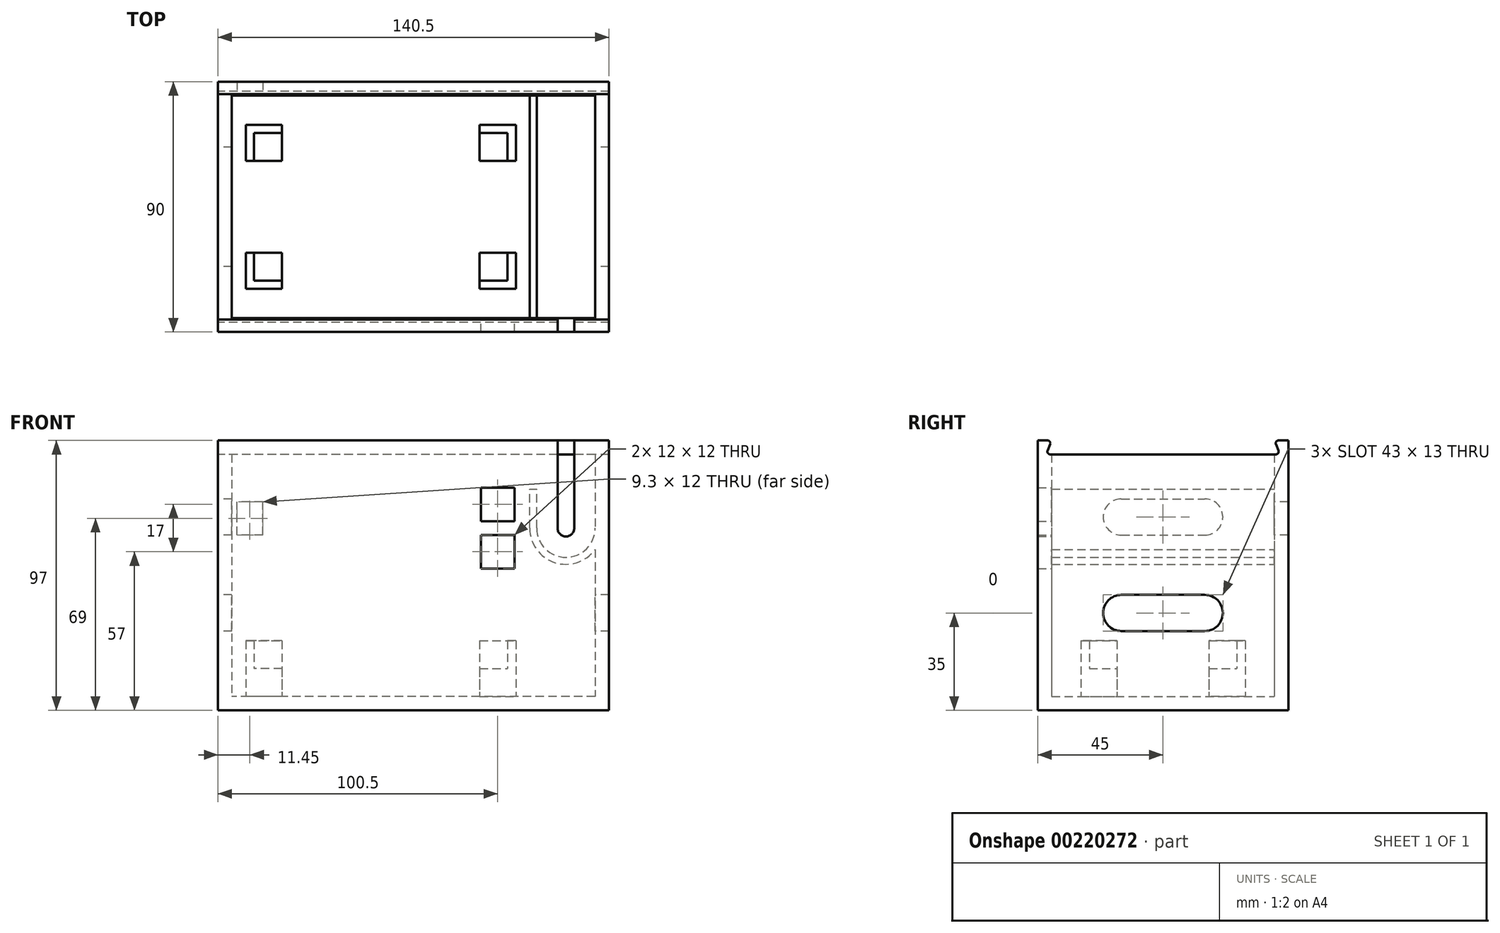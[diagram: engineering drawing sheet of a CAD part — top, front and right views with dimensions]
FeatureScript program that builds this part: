
annotation { "Feature Type Name" : "Feature", "Feature Type Description" : "" }
export const myFeature = defineFeature(function(context is Context, id is Id, definition is map)
    precondition{}
    {
        {
            var Q0;
            Q0=qCreatedBy(makeId("Top.planeOp"),FACE);
            var sketch = newSketch(context, id + "F0", { "sketchPlane" : qUnion([Q0])});
            skLineSegment(sketch, "E0.bottom", {"start": v(70.25, -45) * mm, "end": v(-70.25, -45) * mm});
            skLineSegment(sketch, "E0.top", {"start": v(70.25, 45) * mm, "end": v(-70.25, 45) * mm});
            skLineSegment(sketch, "E0.left", {"start": v(70.25, -45) * mm, "end": v(70.25, 45) * mm});
            skLineSegment(sketch, "E0.right", {"start": v(-70.25, -45) * mm, "end": v(-70.25, 45) * mm});
            skPoint(sketch, "E0.middle", {"position": v(0, 0) * mm});
            skSolve(sketch);
        }
        {
            var Q0;
            Q0=makeQuery(id+"F0.imprint","IMPRINT",FACE,{"disambiguationData":[TD([[makeQuery(id+"F0.imprint","IMPRINT",EDGE,{"derivedFrom":sQuery(id+"F0.wireOp",EDGE,"E0.bottom")}),-1.0]])]});
            extrude(context, id + "F1", {"entities" : qUnion([Q0]), "depth" : 112 * mm});
        }
        {
            var Q0;
            Q0=makeQuery(id+"F1.opExtrude","CAP_FACE",FACE,{"disambiguationData":[OSD([sQuery(id+"F0.wireOp",EDGE,"E0.bottom"),sQuery(id+"F0.wireOp",EDGE,"E0.top"),sQuery(id+"F0.wireOp",EDGE,"E0.left"),sQuery(id+"F0.wireOp",EDGE,"E0.right")])],"isStart":false});
            shell(context, id + "F2", {"entities" : qUnion([Q0]), "thickness" : 5 * mm});
        }
        {
            var Q0;
            Q0=makeQuery(id+"F1.opExtrude","SWEPT_FACE",FACE,{"disambiguationData":[OSD([sQuery(id+"F0.wireOp",EDGE,"E0.right")])]});
            var sketch = newSketch(context, id + "F3", { "sketchPlane" : qUnion([Q0])});
            skLineSegment(sketch, "E1", {"start": v(-40, 107) * mm, "end": v(-40.52, 107) * mm});
            skLineSegment(sketch, "E2", {"start": v(-41.45, 108.37) * mm, "end": v(-40.55, 110.63) * mm});
            skLineSegment(sketch, "E3", {"start": v(40, 107) * mm, "end": v(40.52, 107) * mm});
            skLineSegment(sketch, "E4", {"start": v(41.45, 108.37) * mm, "end": v(40.55, 110.63) * mm});
            skLineSegment(sketch, "E5", {"start": v(-40, 107) * mm, "end": v(40, 107) * mm});
            skArc(sketch, "E6.filletArc", {"start": v(-40.55, 110.63) * mm, "mid": v(-40.65, 111.56) * mm, "end": v(-41.48, 112) * mm});
            skPoint(sketch, "E7.visualSharp", {"position": v(-42, 107) * mm});
            skArc(sketch, "E7.filletArc", {"start": v(-41.45, 108.37) * mm, "mid": v(-41.35, 107.44) * mm, "end": v(-40.52, 107) * mm});
            skArc(sketch, "E8.filletArc", {"start": v(41.48, 112) * mm, "mid": v(40.65, 111.56) * mm, "end": v(40.55, 110.63) * mm});
            skPoint(sketch, "E9.visualSharp", {"position": v(42, 107) * mm});
            skArc(sketch, "E9.filletArc", {"start": v(40.52, 107) * mm, "mid": v(41.35, 107.44) * mm, "end": v(41.45, 108.37) * mm});
            skLineSegment(sketch, "E10", {"start": v(-41.48, 112) * mm, "end": v(41.48, 112) * mm});
            skSolve(sketch);
        }
        {
            var Q0;
            Q0=makeQuery(id+"F3.imprint","IMPRINT",FACE,{"disambiguationData":[TD([[makeQuery(id+"F3.imprint","IMPRINT",EDGE,{"derivedFrom":sQuery(id+"F3.wireOp",EDGE,"E1")}),-1.0]])]});
            extrude(context, id + "F4", {"entities" : qUnion([Q0]), "operationType" : NewBodyOperationType.REMOVE, "oppositeDirection" : true, "depth" : 147.9 * mm});
        }
        {
            var Q0;
            Q0=makeQuery(id+"F2.opShell","OFFSET_FACE",FACE,{"disambiguationData":[OSD([sQuery(id+"F0.wireOp",EDGE,"E0.top")])]});
            var sketch = newSketch(context, id + "F5", { "sketchPlane" : qUnion([Q0])});
            skArc(sketch, "E11", {"start": v(44.25, 80.5) * mm, "mid": v(54.75, 70) * mm, "end": v(65.25, 80.5) * mm});
            skArc(sketch, "E12", {"start": v(41.75, 80.5) * mm, "mid": v(50.72, 68.14) * mm, "end": v(65.25, 72.84) * mm});
            skPoint(sketch, "E13", {"position": v(44.25, 80.5) * mm});
            skPoint(sketch, "E14", {"position": v(41.75, 80.5) * mm});
            skLineSegment(sketch, "E15", {"start": v(44.25, 80.5) * mm, "end": v(44.25, 94.5) * mm});
            skLineSegment(sketch, "E16", {"start": v(41.75, 80.5) * mm, "end": v(41.75, 94.5) * mm});
            skLineSegment(sketch, "E17", {"start": v(41.75, 94.5) * mm, "end": v(44.25, 94.5) * mm});
            skPoint(sketch, "E18", {"position": v(65.25, 80.5) * mm});
            skLineSegment(sketch, "E19", {"start": v(65.25, 80.5) * mm, "end": v(65.25, 72.84) * mm});
            skSolve(sketch);
        }
        {
            var Q0;
            Q0=qSketchRegion(id+"F5",true);
            extrude(context, id + "F6", {"entities" : qUnion([Q0]), "operationType" : NewBodyOperationType.ADD, "depth" : 83.1 * mm});
        }
        {
            var Q0;
            Q0=makeQuery(id+"F2.opShell","OFFSET_FACE",FACE,{"disambiguationData":[OSD([sQuery(id+"F0.wireOp",EDGE,"E0.bottom")])]});
            var sketch = newSketch(context, id + "F7", { "sketchPlane" : qUnion([Q0])});
            skArc(sketch, "E20", {"start": v(-57.75, 80.5) * mm, "mid": v(-54.75, 77.5) * mm, "end": v(-51.75, 80.5) * mm});
            skLineSegment(sketch, "E21", {"start": v(-57.75, 80.5) * mm, "end": v(-57.75, 112.14) * mm});
            skLineSegment(sketch, "E22", {"start": v(-57.75, 112.14) * mm, "end": v(-51.75, 112.14) * mm});
            skLineSegment(sketch, "E23", {"start": v(-51.75, 112.14) * mm, "end": v(-51.75, 80.5) * mm});
            skLineSegment(sketch, "E24", {"start": v(-54.75, 80.5) * mm, "end": v(-36.25, 80.5) * mm});
            skLineSegment(sketch, "E25", {"start": v(-36.25, 80.5) * mm, "end": v(-36.25, 83) * mm});
            skLineSegment(sketch, "E26", {"start": v(-36.25, 80.5) * mm, "end": v(-36.25, 78) * mm});
            skLineSegment(sketch, "E27.bottom", {"start": v(-36.25, 83) * mm, "end": v(-24.25, 83) * mm});
            skLineSegment(sketch, "E27.top", {"start": v(-36.25, 95) * mm, "end": v(-24.25, 95) * mm});
            skLineSegment(sketch, "E27.left", {"start": v(-36.25, 83) * mm, "end": v(-36.25, 95) * mm});
            skLineSegment(sketch, "E27.right", {"start": v(-24.25, 83) * mm, "end": v(-24.25, 95) * mm});
            skLineSegment(sketch, "E28.bottom", {"start": v(-36.25, 78) * mm, "end": v(-24.25, 78) * mm});
            skLineSegment(sketch, "E28.top", {"start": v(-36.25, 66) * mm, "end": v(-24.25, 66) * mm});
            skLineSegment(sketch, "E28.left", {"start": v(-36.25, 78) * mm, "end": v(-36.25, 66) * mm});
            skLineSegment(sketch, "E28.right", {"start": v(-24.25, 78) * mm, "end": v(-24.25, 66) * mm});
            skSolve(sketch);
        }
        {
            var Q0;
            Q0=qSketchRegion(id+"F7",true);
            extrude(context, id + "F8", {"entities" : qUnion([Q0]), "operationType" : NewBodyOperationType.REMOVE, "oppositeDirection" : true, "depth" : 25 * mm});
        }
        {
            var Q0;
            Q0=makeQuery(id+"F2.opShell","OFFSET_FACE",FACE,{"disambiguationData":[OSD([sQuery(id+"F0.wireOp",EDGE,"E0.bottom"),sQuery(id+"F0.wireOp",EDGE,"E0.top"),sQuery(id+"F0.wireOp",EDGE,"E0.left"),sQuery(id+"F0.wireOp",EDGE,"E0.right")])]});
            var sketch = newSketch(context, id + "F9", { "sketchPlane" : qUnion([Q0])});
            skLineSegment(sketch, "E29.bottom", {"start": v(-65.25, 40) * mm, "end": v(65.25, 40) * mm});
            skLineSegment(sketch, "E29.top", {"start": v(-65.25, -40) * mm, "end": v(65.25, -40) * mm});
            skLineSegment(sketch, "E29.left", {"start": v(-65.25, 40) * mm, "end": v(-65.25, -40) * mm});
            skLineSegment(sketch, "E29.right", {"start": v(65.25, 40) * mm, "end": v(65.25, -40) * mm});
            skSolve(sketch);
        }
        {
            var Q0;
            Q0=qSketchRegion(id+"F9",true);
            extrude(context, id + "F10", {"entities" : qUnion([Q0]), "operationType" : NewBodyOperationType.ADD, "depth" : 15 * mm});
        }
        {
            var Q0;
            Q0=makeQuery(id+"F1.opExtrude","SWEPT_FACE",FACE,{"disambiguationData":[OSD([sQuery(id+"F0.wireOp",EDGE,"E0.right")])]});
            var sketch = newSketch(context, id + "F11", { "sketchPlane" : qUnion([Q0])});
            skLineSegment(sketch, "E30.bottom", {"start": v(-45, 0) * mm, "end": v(45, 0) * mm});
            skLineSegment(sketch, "E30.top", {"start": v(-45, 15) * mm, "end": v(45, 15) * mm});
            skLineSegment(sketch, "E30.left", {"start": v(-45, 0) * mm, "end": v(-45, 15) * mm});
            skLineSegment(sketch, "E30.right", {"start": v(45, 0) * mm, "end": v(45, 15) * mm});
            skPoint(sketch, "E31.endSnap0", {"position": v(0, 15) * mm});
            skLineSegment(sketch, "E32.bottom", {"start": v(15, 56.5) * mm, "end": v(-15, 56.5) * mm});
            skLineSegment(sketch, "E32.top", {"start": v(15, 43.5) * mm, "end": v(-15, 43.5) * mm});
            skPoint(sketch, "E32.middle", {"position": v(0, 50) * mm});
            skArc(sketch, "E33", {"start": v(-15, 56.5) * mm, "mid": v(-21.5, 50) * mm, "end": v(-15, 43.5) * mm});
            skArc(sketch, "E34", {"start": v(15, 43.5) * mm, "mid": v(21.5, 50) * mm, "end": v(15, 56.5) * mm});
            skSolve(sketch);
        }
        {
            var Q0;
            Q0=makeQuery(id+"F11.imprint","IMPRINT",FACE,{"disambiguationData":[TD([[makeQuery(id+"F11.imprint","IMPRINT",EDGE,{"derivedFrom":sQuery(id+"F11.wireOp",EDGE,"E30.bottom")}),-1.0]])]});
            var Q1;
            Q1=makeQuery(id+"F11.imprint","IMPRINT",FACE,{"disambiguationData":[TD([[makeQuery(id+"F11.imprint","IMPRINT",EDGE,{"derivedFrom":sQuery(id+"F11.wireOp",EDGE,"E32.bottom")}),1.0]])]});
            extrude(context, id + "F12", {"entities" : qUnion([Q0, Q1]), "operationType" : NewBodyOperationType.REMOVE, "oppositeDirection" : true, "depth" : 174.4 * mm});
        }
        {
            var Q0;
            Q0=makeQuery(id+"F1.opExtrude","SWEPT_FACE",FACE,{"disambiguationData":[OSD([sQuery(id+"F0.wireOp",EDGE,"E0.right")])]});
            var sketch = newSketch(context, id + "F13", { "sketchPlane" : qUnion([Q0])});
            skLineSegment(sketch, "E35.bottom", {"start": v(15, 78) * mm, "end": v(-15, 78) * mm});
            skLineSegment(sketch, "E35.top", {"start": v(15, 91) * mm, "end": v(-15, 91) * mm});
            skPoint(sketch, "E35.middle", {"position": v(0, 84.5) * mm});
            skArc(sketch, "E36", {"start": v(-15, 91) * mm, "mid": v(-21.5, 84.5) * mm, "end": v(-15, 78) * mm});
            skArc(sketch, "E37", {"start": v(15, 78) * mm, "mid": v(21.5, 84.5) * mm, "end": v(15, 91) * mm});
            skSolve(sketch);
        }
        {
            var Q0;
            Q0=makeQuery(id+"F13.imprint","IMPRINT",FACE,{"disambiguationData":[TD([[makeQuery(id+"F13.imprint","IMPRINT",EDGE,{"derivedFrom":sQuery(id+"F13.wireOp",EDGE,"E35.top")}),1.0]])]});
            extrude(context, id + "F14", {"entities" : qUnion([Q0]), "operationType" : NewBodyOperationType.REMOVE, "oppositeDirection" : true, "depth" : 25 * mm});
        }
        {
            var Q0;
            Q0=makeQuery(id+"F10.opExtrude","CAP_FACE",FACE,{"disambiguationData":[OSD([sQuery(id+"F9.wireOp",EDGE,"E29.bottom"),sQuery(id+"F9.wireOp",EDGE,"E29.top"),sQuery(id+"F9.wireOp",EDGE,"E29.left"),sQuery(id+"F9.wireOp",EDGE,"E29.right")])],"isStart":false});
            var sketch = newSketch(context, id + "F15", { "sketchPlane" : qUnion([Q0])});
            skLineSegment(sketch, "E38.bottom", {"start": v(-65.25, 40) * mm, "end": v(41.75, 40) * mm});
            skLineSegment(sketch, "E38.top", {"start": v(-65.25, -40) * mm, "end": v(41.75, -40) * mm});
            skLineSegment(sketch, "E38.left", {"start": v(-65.25, 40) * mm, "end": v(-65.25, -40) * mm});
            skLineSegment(sketch, "E38.right", {"start": v(41.75, 40) * mm, "end": v(41.75, -40) * mm});
            skLineSegment(sketch, "E39", {"start": v(-65.25, -40) * mm, "end": v(-57.25, -40) * mm});
            skLineSegment(sketch, "E40", {"start": v(-47.25, 16.5) * mm, "end": v(-47.25, 29.5) * mm});
            skLineSegment(sketch, "E41", {"start": v(-47.25, 29.5) * mm, "end": v(-60.25, 29.5) * mm});
            skLineSegment(sketch, "E42", {"start": v(-60.25, 29.5) * mm, "end": v(-60.25, 16.5) * mm});
            skLineSegment(sketch, "E43", {"start": v(-60.25, 16.5) * mm, "end": v(-47.25, 16.5) * mm});
            skLineSegment(sketch, "E44.MirrorCS", {"start": v(23.75, 29.5) * mm, "end": v(36.75, 29.5) * mm});
            skLineSegment(sketch, "E45.MirrorCS", {"start": v(36.75, 29.5) * mm, "end": v(36.75, 16.5) * mm});
            skLineSegment(sketch, "E46.MirrorCS", {"start": v(23.75, 16.5) * mm, "end": v(23.75, 29.5) * mm});
            skLineSegment(sketch, "E47.MirrorCS", {"start": v(36.75, 16.5) * mm, "end": v(23.75, 16.5) * mm});
            skLineSegment(sketch, "E48.MirrorCS", {"start": v(-47.25, -29.5) * mm, "end": v(-60.25, -29.5) * mm});
            skLineSegment(sketch, "E49.MirrorCS", {"start": v(-60.25, -29.5) * mm, "end": v(-60.25, -16.5) * mm});
            skLineSegment(sketch, "E50.MirrorCS", {"start": v(-60.25, -16.5) * mm, "end": v(-47.25, -16.5) * mm});
            skLineSegment(sketch, "E51.MirrorCS", {"start": v(-47.25, -16.5) * mm, "end": v(-47.25, -29.5) * mm});
            skLineSegment(sketch, "E52.MirrorCS", {"start": v(23.75, -29.5) * mm, "end": v(36.75, -29.5) * mm});
            skLineSegment(sketch, "E53.MirrorCS", {"start": v(23.75, -16.5) * mm, "end": v(23.75, -29.5) * mm});
            skLineSegment(sketch, "E54.MirrorCS", {"start": v(36.75, -16.5) * mm, "end": v(23.75, -16.5) * mm});
            skLineSegment(sketch, "E55.MirrorCS", {"start": v(36.75, -29.5) * mm, "end": v(36.75, -16.5) * mm});
            skSolve(sketch);
        }
        {
            var Q0;
            Q0=makeQuery(id+"F15.imprint","IMPRINT",FACE,{"disambiguationData":[TD([[makeQuery(id+"F15.imprint","IMPRINT",EDGE,{"derivedFrom":sQuery(id+"F15.wireOp",EDGE,"E40")}),1.0]])]});
            var Q1;
            Q1=makeQuery(id+"F15.imprint","IMPRINT",FACE,{"disambiguationData":[TD([[makeQuery(id+"F15.imprint","IMPRINT",EDGE,{"derivedFrom":sQuery(id+"F15.wireOp",EDGE,"E44.MirrorCS")}),-1.0]])]});
            var Q2;
            Q2=makeQuery(id+"F15.imprint","IMPRINT",FACE,{"disambiguationData":[TD([[makeQuery(id+"F15.imprint","IMPRINT",EDGE,{"derivedFrom":sQuery(id+"F15.wireOp",EDGE,"E52.MirrorCS")}),1.0]])]});
            var Q3;
            Q3=makeQuery(id+"F15.imprint","IMPRINT",FACE,{"disambiguationData":[TD([[makeQuery(id+"F15.imprint","IMPRINT",EDGE,{"derivedFrom":sQuery(id+"F15.wireOp",EDGE,"E48.MirrorCS")}),-1.0]])]});
            extrude(context, id + "F16", {"entities" : qUnion([Q0, Q1, Q2, Q3]), "operationType" : NewBodyOperationType.ADD, "depth" : 10 * mm});
        }
        {
            var Q0;
            Q0=makeQuery(id+"F16.opExtrude","CAP_FACE",FACE,{"disambiguationData":[OSD([sQuery(id+"F15.wireOp",EDGE,"E44.MirrorCS"),sQuery(id+"F15.wireOp",EDGE,"E45.MirrorCS"),sQuery(id+"F15.wireOp",EDGE,"E46.MirrorCS"),sQuery(id+"F15.wireOp",EDGE,"E47.MirrorCS")])],"isStart":false});
            var sketch = newSketch(context, id + "F17", { "sketchPlane" : qUnion([Q0])});
            skLineSegment(sketch, "E56", {"start": v(-60.25, 29.5) * mm, "end": v(-47.25, 29.5) * mm});
            skLineSegment(sketch, "E57", {"start": v(-47.25, 29.5) * mm, "end": v(-47.25, 26.5) * mm});
            skLineSegment(sketch, "E58", {"start": v(-47.25, 26.5) * mm, "end": v(-57.25, 26.5) * mm});
            skLineSegment(sketch, "E59", {"start": v(-57.25, 26.5) * mm, "end": v(-57.25, 16.5) * mm});
            skLineSegment(sketch, "E60", {"start": v(-57.25, 16.5) * mm, "end": v(-60.25, 16.5) * mm});
            skLineSegment(sketch, "E61", {"start": v(-60.25, 16.5) * mm, "end": v(-60.25, 29.5) * mm});
            skLineSegment(sketch, "E62.MirrorCS", {"start": v(-47.25, -29.5) * mm, "end": v(-47.25, -26.5) * mm});
            skLineSegment(sketch, "E63.MirrorCS", {"start": v(-57.25, -16.5) * mm, "end": v(-60.25, -16.5) * mm});
            skLineSegment(sketch, "E64.MirrorCS", {"start": v(-60.25, -29.5) * mm, "end": v(-47.25, -29.5) * mm});
            skLineSegment(sketch, "E65.MirrorCS", {"start": v(-47.25, -26.5) * mm, "end": v(-57.25, -26.5) * mm});
            skLineSegment(sketch, "E66.MirrorCS", {"start": v(-57.25, -26.5) * mm, "end": v(-57.25, -16.5) * mm});
            skLineSegment(sketch, "E67.MirrorCS", {"start": v(-60.25, -16.5) * mm, "end": v(-60.25, -29.5) * mm});
            skLineSegment(sketch, "E68.MirrorCS", {"start": v(33.75, 16.5) * mm, "end": v(36.75, 16.5) * mm});
            skLineSegment(sketch, "E69.MirrorCS", {"start": v(23.75, 29.5) * mm, "end": v(23.75, 26.5) * mm});
            skLineSegment(sketch, "E70.MirrorCS", {"start": v(33.75, 26.5) * mm, "end": v(33.75, 16.5) * mm});
            skLineSegment(sketch, "E71.MirrorCS", {"start": v(23.75, 26.5) * mm, "end": v(33.75, 26.5) * mm});
            skLineSegment(sketch, "E72.MirrorCS", {"start": v(36.75, 29.5) * mm, "end": v(23.75, 29.5) * mm});
            skLineSegment(sketch, "E73.MirrorCS", {"start": v(36.75, 16.5) * mm, "end": v(36.75, 29.5) * mm});
            skLineSegment(sketch, "E74.MirrorCS", {"start": v(23.75, -29.5) * mm, "end": v(23.75, -26.5) * mm});
            skLineSegment(sketch, "E75.MirrorCS", {"start": v(33.75, -16.5) * mm, "end": v(36.75, -16.5) * mm});
            skLineSegment(sketch, "E76.MirrorCS", {"start": v(36.75, -16.5) * mm, "end": v(36.75, -29.5) * mm});
            skLineSegment(sketch, "E77.MirrorCS", {"start": v(33.75, -26.5) * mm, "end": v(33.75, -16.5) * mm});
            skLineSegment(sketch, "E78.MirrorCS", {"start": v(23.75, -26.5) * mm, "end": v(33.75, -26.5) * mm});
            skLineSegment(sketch, "E79.MirrorCS", {"start": v(36.75, -29.5) * mm, "end": v(23.75, -29.5) * mm});
            skSolve(sketch);
        }
        {
            var Q0;
            Q0=qSketchRegion(id+"F17",true);
            extrude(context, id + "F18", {"entities" : qUnion([Q0]), "operationType" : NewBodyOperationType.ADD, "depth" : 10 * mm});
        }
        {
            var Q0;
            Q0=qCreatedBy(makeId("Front.planeOp"),FACE);
            var sketch = newSketch(context, id + "F19", { "sketchPlane" : qUnion([Q0])});
            skLineSegment(sketch, "E80", {"start": v(-63.45, 78) * mm, "end": v(-58.95, 78) * mm});
            skLineSegment(sketch, "E81.bottom", {"start": v(-54.15, 78) * mm, "end": v(-63.45, 78) * mm});
            skLineSegment(sketch, "E81.top", {"start": v(-54.15, 90) * mm, "end": v(-63.45, 90) * mm});
            skLineSegment(sketch, "E81.left", {"start": v(-54.15, 78) * mm, "end": v(-54.15, 90) * mm});
            skLineSegment(sketch, "E81.right", {"start": v(-63.45, 78) * mm, "end": v(-63.45, 90) * mm});
            skPoint(sketch, "E82.orphan", {"position": v(-69.35, 78) * mm});
            skSolve(sketch);
        }
        {
            var Q0;
            Q0=qSketchRegion(id+"F19",true);
            extrude(context, id + "F20", {"entities" : qUnion([Q0]), "operationType" : NewBodyOperationType.REMOVE, "oppositeDirection" : true, "depth" : 61.2 * mm});
        }
    });
